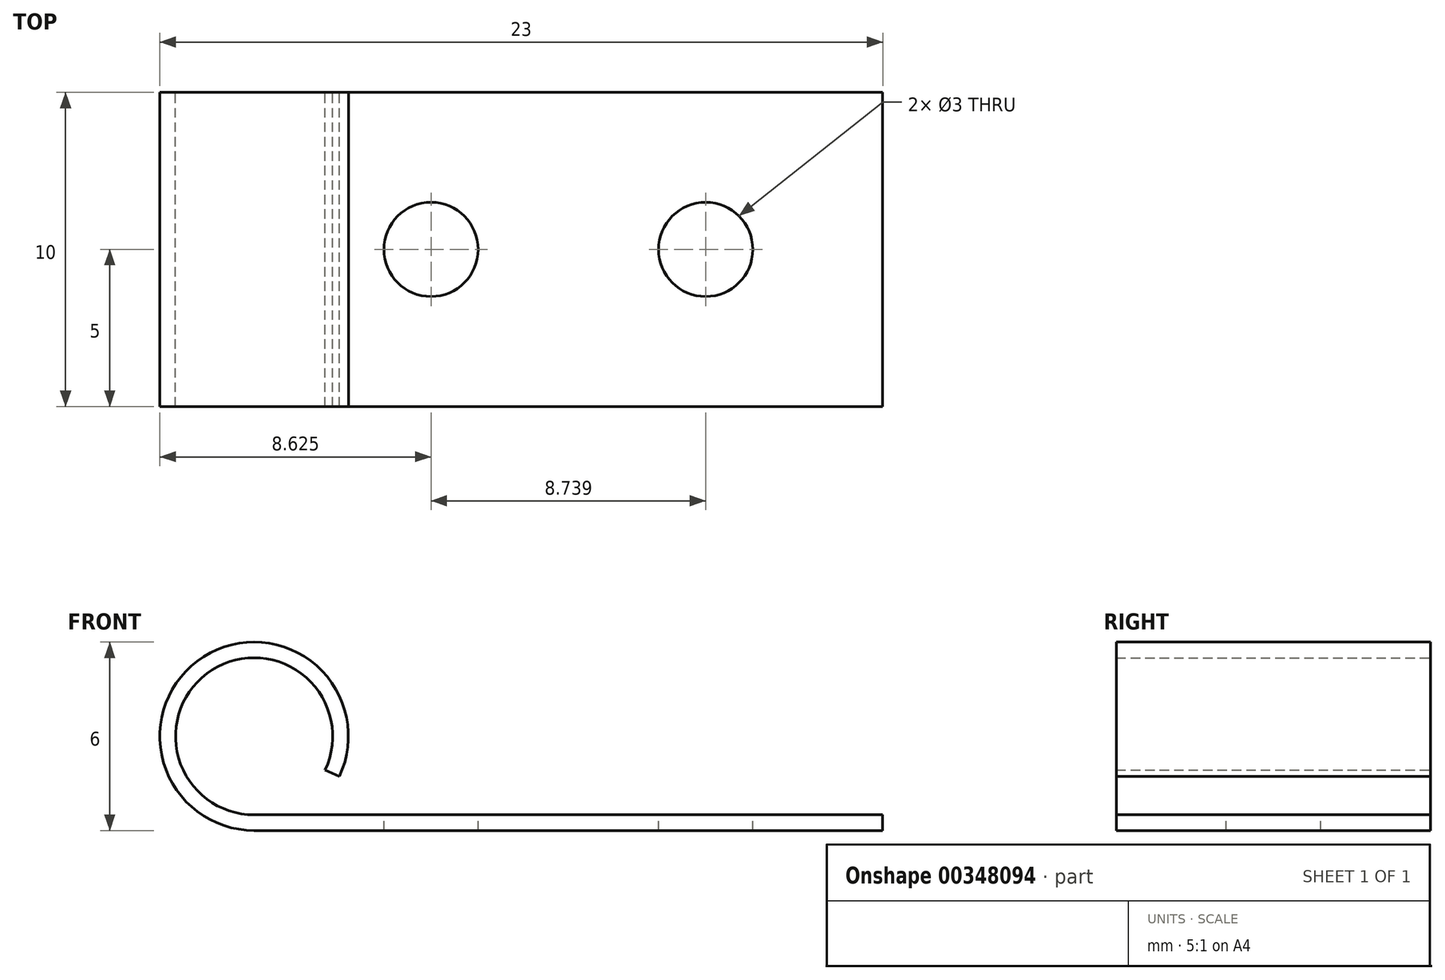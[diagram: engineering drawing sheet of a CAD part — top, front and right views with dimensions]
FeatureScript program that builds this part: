
annotation { "Feature Type Name" : "Feature", "Feature Type Description" : "" }
export const myFeature = defineFeature(function(context is Context, id is Id, definition is map)
    precondition{}
    {
        {
            var Q0;
            Q0=qCreatedBy(makeId("Front.planeOp"),FACE);
            var sketch = newSketch(context, id + "F0", { "sketchPlane" : qUnion([Q0])});
            skLineSegment(sketch, "E0", {"start": v(10.82, 25.94) * mm, "end": v(30.82, 25.94) * mm});
            skArc(sketch, "E1", {"start": v(13.53, 27.66) * mm, "mid": v(9.21, 31.47) * mm, "end": v(10.82, 25.94) * mm});
            skArc(sketch, "E2.0", {"start": v(13.08, 27.87) * mm, "mid": v(9.48, 31.05) * mm, "end": v(10.82, 26.44) * mm});
            skLineSegment(sketch, "E3.0", {"start": v(10.82, 26.44) * mm, "end": v(30.82, 26.44) * mm});
            skLineSegment(sketch, "E4", {"start": v(13.53, 27.66) * mm, "end": v(13.08, 27.87) * mm});
            skLineSegment(sketch, "E5", {"start": v(30.82, 25.94) * mm, "end": v(30.82, 26.44) * mm});
            skSolve(sketch);
        }
        {
            var Q0;
            Q0=makeQuery(id+"F0.imprint","IMPRINT",FACE,{"disambiguationData":[TD([[makeQuery(id+"F0.imprint","IMPRINT",EDGE,{"derivedFrom":sQuery(id+"F0.wireOp",EDGE,"E0")}),1.0]])]});
            extrude(context, id + "F1", {"entities" : qUnion([Q0]), "depth" : 10 * mm});
        }
        {
            var Q0;
            Q0=makeQuery(id+"F1.opExtrude","SWEPT_FACE",FACE,{"disambiguationData":[OSD([sQuery(id+"F0.wireOp",EDGE,"E3.0")])]});
            var sketch = newSketch(context, id + "F2", { "sketchPlane" : qUnion([Q0])});
            skPoint(sketch, "E6", {"position": v(16.45, -5) * mm});
            skPoint(sketch, "E7", {"position": v(25.18, -5) * mm});
            skSolve(sketch);
        }
        {
            var Q0;
            Q0=sQuery(id+"F2.wireOp",VERTEX,"E6");
            var Q1;
            Q1=sQuery(id+"F2.wireOp",VERTEX,"E7");
            var Q2;
            Q2=makeQuery(id+"F1.opExtrude","SWEPT_BODY",BODY,{"disambiguationData":[OSD([sQuery(id+"F0.wireOp",EDGE,"E0"),sQuery(id+"F0.wireOp",EDGE,"E1"),sQuery(id+"F0.wireOp",EDGE,"E2.0"),sQuery(id+"F0.wireOp",EDGE,"E3.0"),sQuery(id+"F0.wireOp",EDGE,"E4"),sQuery(id+"F0.wireOp",EDGE,"E5")])]});
            hole(context, id + "F3", {"style" : HoleStyle.SIMPLE, "endStyle" : HoleEndStyle.THROUGH, "holeDiameter" : 3 * mm, "isTappedThrough" : true, "tappedDepth" : 12 * mm, "tapClearance" : 3, "locations" : qUnion([Q0, Q1]), "scope" : qUnion([Q2])});
        }
    });
